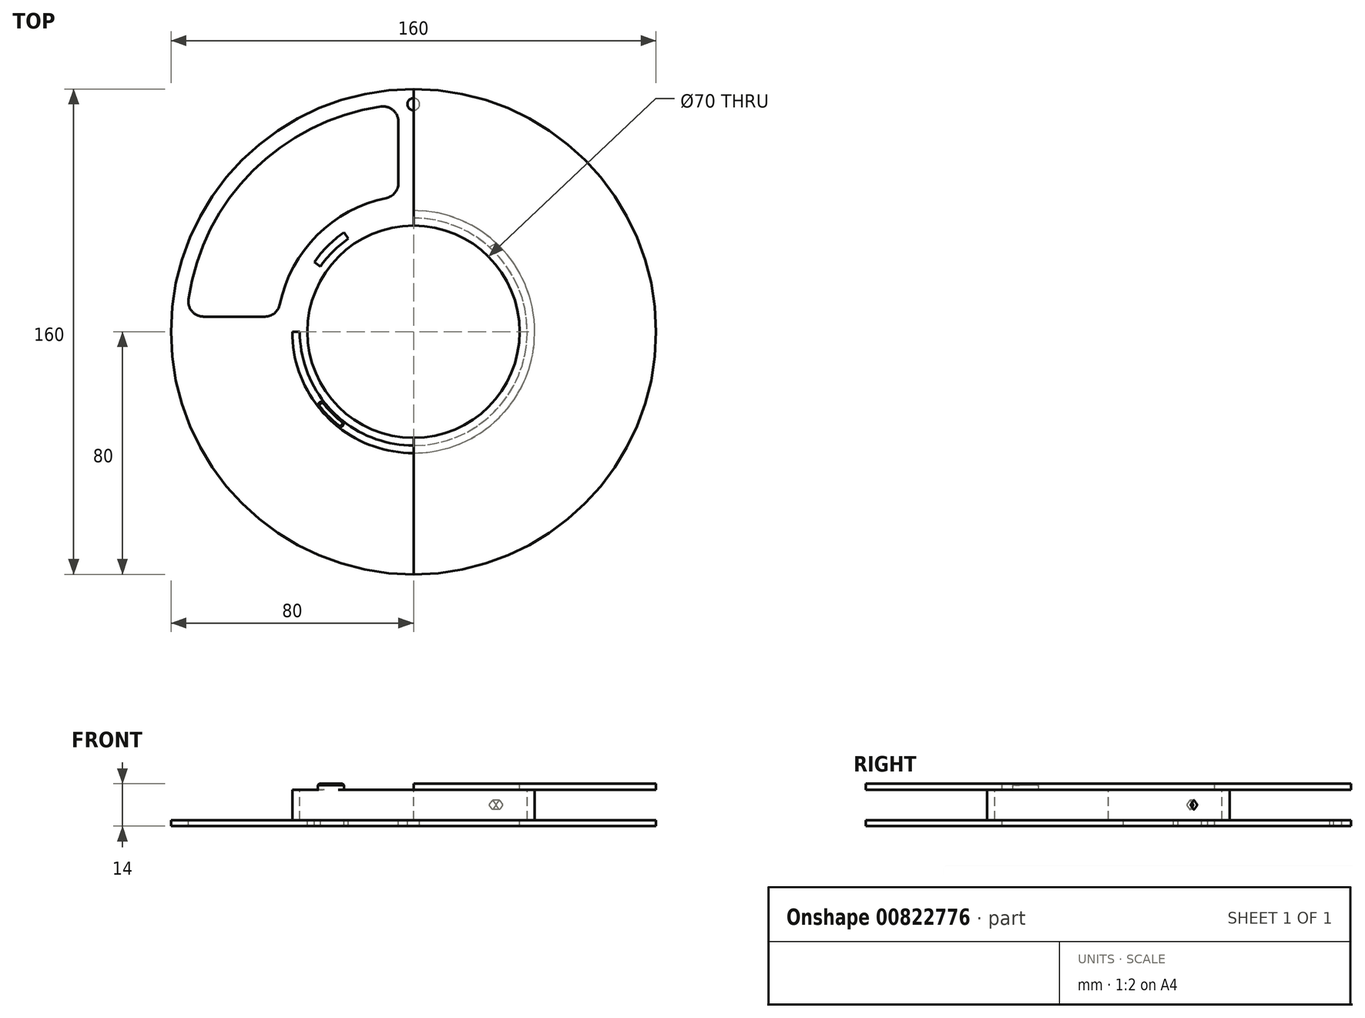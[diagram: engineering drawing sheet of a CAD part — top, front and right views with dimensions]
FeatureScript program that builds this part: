
annotation { "Feature Type Name" : "Feature", "Feature Type Description" : "" }
export const myFeature = defineFeature(function(context is Context, id is Id, definition is map)
    precondition{}
    {
        {
            var Q0;
            Q0=qCreatedBy(makeId("Front.planeOp"),FACE);
            var sketch = newSketch(context, id + "F0", { "sketchPlane" : qUnion([Q0])});
            skLineSegment(sketch, "E0", {"start": v(0, 7) * mm, "end": v(-80, 7) * mm});
            skLineSegment(sketch, "E1", {"start": v(-80, 7) * mm, "end": v(-80, 5) * mm});
            skLineSegment(sketch, "E2", {"start": v(-80, 5) * mm, "end": v(-40, 5) * mm});
            skLineSegment(sketch, "E3", {"start": v(-40, 5) * mm, "end": v(-40, 0) * mm});
            skLineSegment(sketch, "E4", {"start": v(-37.5, 0) * mm, "end": v(-37.5, 5) * mm});
            skLineSegment(sketch, "E5", {"start": v(-37.5, 5) * mm, "end": v(0, 5) * mm});
            skLineSegment(sketch, "E6", {"start": v(0, 5) * mm, "end": v(0, 7) * mm});
            skLineSegment(sketch, "E7.MirrorCS", {"start": v(-80, -7) * mm, "end": v(-80, -5) * mm});
            skLineSegment(sketch, "E8.MirrorCS", {"start": v(0, -7) * mm, "end": v(-80, -7) * mm});
            skLineSegment(sketch, "E9.MirrorCS", {"start": v(-80, -5) * mm, "end": v(-40, -5) * mm});
            skLineSegment(sketch, "E10.MirrorCS", {"start": v(-40, -5) * mm, "end": v(-40, 0) * mm});
            skLineSegment(sketch, "E11.MirrorCS", {"start": v(-37.5, 0) * mm, "end": v(-37.5, -5) * mm});
            skLineSegment(sketch, "E12.MirrorCS", {"start": v(-37.5, -5) * mm, "end": v(0, -5) * mm});
            skLineSegment(sketch, "E13.MirrorCS", {"start": v(0, -5) * mm, "end": v(0, -7) * mm});
            skLineSegment(sketch, "E14", {"start": v(0, 7) * mm, "end": v(0, -7) * mm, "construction": true});
            skSolve(sketch);
        }
        {
            var Q0;
            Q0=qSketchRegion(id+"F0",true);
            var Q1;
            Q1=sQuery(id+"F0.wireOp",EDGE,"E14");
            revolve(context, id + "F1", {"entities" : qUnion([Q0]), "axis" : qUnion([Q1]), "revolveType" : RevolveType.FULL});
        }
        {
            var Q0;
            Q0=makeQuery(id+"F1.opRevolve","SWEPT_FACE",FACE,{"disambiguationData":[OSD([sQuery(id+"F0.wireOp",EDGE,"E0")])]});
            var sketch = newSketch(context, id + "F2", { "sketchPlane" : qUnion([Q0])});
            skLineSegment(sketch, "E15", {"start": v(-40, 0) * mm, "end": v(-80, 0) * mm, "construction": true});
            skPoint(sketch, "E16.orphan", {"position": v(80, 0) * mm});
            skPoint(sketch, "E17.0.start.orphan", {"position": v(0, -80) * mm});
            skArc(sketch, "E18.0", {"start": v(0, 40) * mm, "mid": v(-28.28, 28.28) * mm, "end": v(-40, 0) * mm, "construction": true});
            skArc(sketch, "E19.1", {"start": v(-9, 44.1) * mm, "mid": v(-31.82, 31.82) * mm, "end": v(-44.1, 9) * mm});
            skLineSegment(sketch, "E20", {"start": v(0, 80) * mm, "end": v(0, 40) * mm, "construction": true});
            skPoint(sketch, "E21.visualSharp", {"position": v(-44.72, 5) * mm});
            skArc(sketch, "E21.filletArc", {"start": v(-48.99, 5) * mm, "mid": v(-45.83, 6.13) * mm, "end": v(-44.1, 9) * mm});
            skPoint(sketch, "E22.visualSharp", {"position": v(-73.21, 5) * mm});
            skPoint(sketch, "E23.visualSharp", {"position": v(-5, 73.21) * mm});
            skPoint(sketch, "E24.visualSharp", {"position": v(-5, 44.72) * mm});
            skArc(sketch, "E24.filletArc", {"start": v(-9, 44.1) * mm, "mid": v(-6.13, 45.83) * mm, "end": v(-5, 48.99) * mm});
            skArc(sketch, "E25", {"start": v(0, 80) * mm, "mid": v(-56.57, 56.57) * mm, "end": v(-80, 0) * mm, "construction": true});
            skArc(sketch, "E26.0", {"start": v(-10.71, 74.23) * mm, "mid": v(-53.03, 53.03) * mm, "end": v(-74.23, 10.71) * mm});
            skLineSegment(sketch, "E27", {"start": v(-48.99, 5) * mm, "end": v(-69.28, 5) * mm});
            skLineSegment(sketch, "E28", {"start": v(-5, 48.99) * mm, "end": v(-5, 69.28) * mm});
            skArc(sketch, "E29.filletArc", {"start": v(-5, 69.28) * mm, "mid": v(-6.73, 73.06) * mm, "end": v(-10.71, 74.23) * mm});
            skArc(sketch, "E30.filletArc", {"start": v(-74.23, 10.71) * mm, "mid": v(-73.06, 6.73) * mm, "end": v(-69.28, 5) * mm});
            skSolve(sketch);
        }
        {
            var Q0;
            Q0=qSketchRegion(id+"F2",true);
            extrude(context, id + "F3", {"entities" : qUnion([Q0]), "operationType" : NewBodyOperationType.REMOVE, "endBound" : BoundingType.THROUGH_ALL, "oppositeDirection" : true, "depth" : 25 * mm});
        }
        {
            var Q0;
            Q0=sQuery(id+"F2.wireOp",VERTEX,"E18.0.center");
            var Q1;
            Q1=makeQuery(id+"F1.opRevolve","SWEPT_BODY",BODY,{"disambiguationData":[OSD([sQuery(id+"F0.wireOp",EDGE,"E0"),sQuery(id+"F0.wireOp",EDGE,"E1"),sQuery(id+"F0.wireOp",EDGE,"E2"),sQuery(id+"F0.wireOp",EDGE,"E3"),sQuery(id+"F0.wireOp",EDGE,"E4"),sQuery(id+"F0.wireOp",EDGE,"E5"),sQuery(id+"F0.wireOp",EDGE,"E6"),sQuery(id+"F0.wireOp",EDGE,"E7.MirrorCS"),sQuery(id+"F0.wireOp",EDGE,"E8.MirrorCS"),sQuery(id+"F0.wireOp",EDGE,"E9.MirrorCS"),sQuery(id+"F0.wireOp",EDGE,"E10.MirrorCS"),sQuery(id+"F0.wireOp",EDGE,"E11.MirrorCS"),sQuery(id+"F0.wireOp",EDGE,"E12.MirrorCS"),sQuery(id+"F0.wireOp",EDGE,"E13.MirrorCS")])]});
            hole(context, id + "F4", {"style" : HoleStyle.SIMPLE, "endStyle" : HoleEndStyle.THROUGH, "holeDiameter" : 70 * mm, "isTappedThrough" : true, "tappedDepth" : 38.4 * mm, "tapClearance" : 3, "locations" : qUnion([Q0]), "scope" : qUnion([Q1])});
        }
        {
            var Q0;
            Q0=makeQuery(id+"F2.imprint","IMPRINT",FACE,{"disambiguationData":[TD([[makeQuery(id+"F2.imprint","IMPRINT",EDGE,{"derivedFrom":sQuery(id+"F2.wireOp",EDGE,"E19.1")}),1.0]])]});
            var sketch = newSketch(context, id + "F5", { "sketchPlane" : qUnion([Q0])});
            skLineSegment(sketch, "E31", {"start": v(0, 80) * mm, "end": v(0, 0) * mm});
            skLineSegment(sketch, "E32", {"start": v(0, 0) * mm, "end": v(-80, 0) * mm});
            skLineSegment(sketch, "E33", {"start": v(-80, 0) * mm, "end": v(-80, 80) * mm});
            skLineSegment(sketch, "E34", {"start": v(-80, 80) * mm, "end": v(0, 80) * mm});
            skSolve(sketch);
        }
        {
            var Q0;
            Q0=qSketchRegion(id+"F5",true);
            var Q1;
            Q1=makeQuery(id+"F1.opRevolve","SWEPT_FACE",FACE,{"disambiguationData":[OSD([sQuery(id+"F0.wireOp",EDGE,"E9.MirrorCS")])]});
            extrude(context, id + "F6", {"entities" : qUnion([Q0]), "operationType" : NewBodyOperationType.REMOVE, "endBound" : BoundingType.UP_TO_SURFACE, "oppositeDirection" : true, "endBoundEntityFace" : qUnion([Q1]), "depth" : 25 * mm});
        }
        {
            var Q0;
            Q0=qCreatedBy(makeId("Right.planeOp"),FACE);
            var sketch = newSketch(context, id + "F7", { "sketchPlane" : qUnion([Q0])});
            skPoint(sketch, "E35.0", {"position": v(80, 7) * mm});
            skPoint(sketch, "E36.0", {"position": v(-80, 5) * mm});
            skLineSegment(sketch, "E37.bottom", {"start": v(-80, 5) * mm, "end": v(80, 5) * mm, "construction": true});
            skLineSegment(sketch, "E37.top", {"start": v(-80, 7) * mm, "end": v(80, 7) * mm, "construction": true});
            skLineSegment(sketch, "E37.left", {"start": v(-80, 5) * mm, "end": v(-80, 7) * mm, "construction": true});
            skLineSegment(sketch, "E37.right", {"start": v(80, 5) * mm, "end": v(80, 7) * mm, "construction": true});
            skLineSegment(sketch, "E38.bottom", {"start": v(80, 7) * mm, "end": v(-80, 7) * mm});
            skLineSegment(sketch, "E38.top", {"start": v(80, 5) * mm, "end": v(-80, 5) * mm});
            skLineSegment(sketch, "E38.left", {"start": v(80, 7) * mm, "end": v(80, 5) * mm});
            skLineSegment(sketch, "E38.right", {"start": v(-80, 7) * mm, "end": v(-80, 5) * mm});
            skSolve(sketch);
        }
        {
            var Q0;
            Q0=qSketchRegion(id+"F7",true);
            extrude(context, id + "F8", {"entities" : qUnion([Q0]), "operationType" : NewBodyOperationType.REMOVE, "endBound" : BoundingType.THROUGH_ALL, "oppositeDirection" : true, "depth" : 25 * mm});
        }
        {
            var Q0;
            {var subQ0=sQuery(id+"F0.wireOp",EDGE,"E12.MirrorCS");var subQ1=sQuery(id+"F0.wireOp",EDGE,"E9.MirrorCS");Q0=makeQuery(id+"F5vmHWThCkjWJyu_1.1.F6.boolean.opBoolean","MERGE",FACE,{"derivedFrom":[makeQuery(id+"F6.boolean.opBoolean","MERGE",FACE,{"derivedFrom":[makeQuery(id+"F1.opRevolve","SWEPT_FACE",FACE,{"disambiguationData":[OSD([subQ1])]}),makeQuery(id+"F1.opRevolve","SWEPT_FACE",FACE,{"disambiguationData":[OSD([subQ0])]}),makeQuery(id+"F6.opExtrude","CAP_FACE",FACE,{"disambiguationData":[OSD([subQ1])],"isStart":false})]}),makeQuery(id+"F5vmHWThCkjWJyu_1.1.F6.opExtrude","CAP_FACE",FACE,{"disambiguationData":[OSD([subQ1,subQ0])],"isStart":false})]});}
            var sketch = newSketch(context, id + "F9", { "sketchPlane" : qUnion([Q0])});
            skArc(sketch, "E39.0", {"start": v(0, 40) * mm, "mid": v(-28.28, 28.28) * mm, "end": v(-40, 0) * mm, "construction": true});
            skLineSegment(sketch, "E40", {"start": v(0, 0) * mm, "end": v(-28.28, 28.28) * mm, "construction": true});
            skArc(sketch, "E41", {"start": v(-28.28, 28.28) * mm, "mid": v(-25.71, 30.64) * mm, "end": v(-22.94, 32.77) * mm});
            skArc(sketch, "E42.0", {"start": v(37.5, 0) * mm, "mid": v(26.52, 26.52) * mm, "end": v(0, 37.5) * mm, "construction": true});
            skArc(sketch, "E43", {"start": v(0, 37.5) * mm, "mid": v(-26.52, 26.52) * mm, "end": v(-37.5, 0) * mm, "construction": true});
            skLineSegment(sketch, "E44", {"start": v(-22.94, 32.77) * mm, "end": v(0, 0) * mm, "construction": true});
            skArc(sketch, "E45", {"start": v(-26.52, 26.52) * mm, "mid": v(-24.1, 28.73) * mm, "end": v(-21.5, 30.72) * mm});
            skArc(sketch, "E46.MirrorCS", {"start": v(-37.5, 0) * mm, "mid": v(-26.52, 26.52) * mm, "end": v(0, 37.5) * mm, "construction": true});
            skArc(sketch, "E47.MirrorCS", {"start": v(-40, 0) * mm, "mid": v(-28.28, 28.28) * mm, "end": v(0, 40) * mm, "construction": true});
            skArc(sketch, "E48", {"start": v(-32.77, 22.94) * mm, "mid": v(-30.64, 25.71) * mm, "end": v(-28.28, 28.28) * mm});
            skLineSegment(sketch, "E49", {"start": v(-32.77, 22.94) * mm, "end": v(0, 0) * mm, "construction": true});
            skArc(sketch, "E50", {"start": v(-30.72, 21.5) * mm, "mid": v(-28.73, 24.1) * mm, "end": v(-26.52, 26.52) * mm});
            skLineSegment(sketch, "E51", {"start": v(-30.72, 21.5) * mm, "end": v(-32.77, 22.94) * mm});
            skLineSegment(sketch, "E52", {"start": v(-22.94, 32.77) * mm, "end": v(-21.5, 30.72) * mm});
            skSolve(sketch);
        }
        {
            var Q0;
            Q0=qSketchRegion(id+"F9",true);
            extrude(context, id + "F10", {"entities" : qUnion([Q0]), "operationType" : NewBodyOperationType.REMOVE, "endBound" : BoundingType.THROUGH_ALL, "oppositeDirection" : true, "depth" : 25 * mm});
        }
        {
            var Q0;
            Q0=makeQuery(id+"F2.imprint","IMPRINT",FACE,{"disambiguationData":[TD([[makeQuery(id+"F2.imprint","IMPRINT",EDGE,{"derivedFrom":sQuery(id+"F2.wireOp",EDGE,"E19.1")}),1.0]])]});
            var sketch = newSketch(context, id + "F11", { "sketchPlane" : qUnion([Q0])});
            skArc(sketch, "E53.0", {"start": v(-37.5, 0) * mm, "mid": v(-26.52, -26.52) * mm, "end": v(0, -37.5) * mm, "construction": true});
            skArc(sketch, "E54.0", {"start": v(-40, 0) * mm, "mid": v(-28.28, -28.28) * mm, "end": v(0, -40) * mm, "construction": true});
            skLineSegment(sketch, "E55", {"start": v(-28.28, -28.28) * mm, "end": v(0, 0) * mm, "construction": true});
            skLineSegment(sketch, "E56", {"start": v(-24.07, -31.95) * mm, "end": v(0, 0) * mm, "construction": true});
            skLineSegment(sketch, "E57", {"start": v(-31.95, -24.07) * mm, "end": v(0, 0) * mm, "construction": true});
            skArc(sketch, "E58", {"start": v(-24.07, -31.95) * mm, "mid": v(-28.28, -28.28) * mm, "end": v(-31.95, -24.07) * mm});
            skArc(sketch, "E59", {"start": v(-22.57, -29.95) * mm, "mid": v(-26.52, -26.52) * mm, "end": v(-29.95, -22.57) * mm});
            skLineSegment(sketch, "E60", {"start": v(-31.95, -24.07) * mm, "end": v(-29.95, -22.57) * mm});
            skLineSegment(sketch, "E61", {"start": v(-22.57, -29.95) * mm, "end": v(-24.07, -31.95) * mm});
            skSolve(sketch);
        }
        {
            var Q0;
            Q0=qSketchRegion(id+"F11",true);
            var Q1;
            Q1=makeQuery(id+"F8.boolean.opBoolean","COPY",FACE,{"derivedFrom":makeQuery(id+"F8.opExtrude","SWEPT_FACE",FACE,{"disambiguationData":[OSD([sQuery(id+"F7.wireOp",EDGE,"E38.top")])]})});
            extrude(context, id + "F12", {"entities" : qUnion([Q0]), "operationType" : NewBodyOperationType.ADD, "endBound" : BoundingType.UP_TO_SURFACE, "oppositeDirection" : true, "endBoundEntityFace" : qUnion([Q1]), "depth" : 25 * mm});
        }
        {
            var Q0;
            Q0=makeQuery(id+"F12.opExtrude","SWEPT_EDGE",EDGE,{"disambiguationData":[OSD([sQuery(id+"F11.wireOp",EDGE,"E58"),sQuery(id+"F11.wireOp",EDGE,"E60")])]});
            var Q1;
            Q1=makeQuery(id+"F12.opExtrude","SWEPT_EDGE",EDGE,{"disambiguationData":[OSD([sQuery(id+"F11.wireOp",EDGE,"E58"),sQuery(id+"F11.wireOp",EDGE,"E61")])]});
            var Q2;
            Q2=makeQuery(id+"F12.opExtrude","SWEPT_EDGE",EDGE,{"disambiguationData":[OSD([sQuery(id+"F11.wireOp",EDGE,"E59"),sQuery(id+"F11.wireOp",EDGE,"E60")])]});
            var Q3;
            Q3=makeQuery(id+"F12.opExtrude","SWEPT_EDGE",EDGE,{"disambiguationData":[OSD([sQuery(id+"F11.wireOp",EDGE,"E59"),sQuery(id+"F11.wireOp",EDGE,"E61")])]});
            fillet(context, id + "F13", {"entities" : qUnion([Q0, Q1, Q2, Q3]), "radius" : 1 * mm, "tangentPropagation" : true, "allowEdgeOverflow" : false});
        }
        {
            var Q0;
            Q0=makeQuery(id+"F12.opExtrude","CAP_EDGE",EDGE,{"disambiguationData":[OSD([sQuery(id+"F11.wireOp",EDGE,"E58")])],"isStart":true});
            var Q1;
            Q1=makeQuery(id+"F12.opExtrude","CAP_EDGE",EDGE,{"disambiguationData":[OSD([sQuery(id+"F11.wireOp",EDGE,"E59")])],"isStart":true});
            var Q2;
            Q2=makeQuery(id+"F12.opExtrude","CAP_EDGE",EDGE,{"disambiguationData":[OSD([sQuery(id+"F11.wireOp",EDGE,"E61")])],"isStart":true});
            var Q3;
            Q3=makeQuery(id+"F12.opExtrude","CAP_EDGE",EDGE,{"disambiguationData":[OSD([sQuery(id+"F11.wireOp",EDGE,"E60")])],"isStart":true});
            var Q4;
            Q4=makeQuery(id+"F10.boolean.opBoolean","COPY",EDGE,{"derivedFrom":makeQuery(id+"F10.opExtrude","CAP_EDGE",EDGE,{"disambiguationData":[OSD([sQuery(id+"F9.wireOp",EDGE,"E45"),sQuery(id+"F9.wireOp",EDGE,"E50")])],"isStart":true})});
            var Q5;
            Q5=makeQuery(id+"F10.boolean.opBoolean","COPY",EDGE,{"derivedFrom":makeQuery(id+"F10.opExtrude","CAP_EDGE",EDGE,{"disambiguationData":[OSD([sQuery(id+"F9.wireOp",EDGE,"E51")])],"isStart":true})});
            var Q6;
            Q6=makeQuery(id+"F10.boolean.opBoolean","COPY",EDGE,{"derivedFrom":makeQuery(id+"F10.opExtrude","CAP_EDGE",EDGE,{"disambiguationData":[OSD([sQuery(id+"F9.wireOp",EDGE,"E41"),sQuery(id+"F9.wireOp",EDGE,"E48")])],"isStart":true})});
            var Q7;
            Q7=makeQuery(id+"F10.boolean.opBoolean","COPY",EDGE,{"derivedFrom":makeQuery(id+"F10.opExtrude","CAP_EDGE",EDGE,{"disambiguationData":[OSD([sQuery(id+"F9.wireOp",EDGE,"E52")])],"isStart":true})});
            chamfer(context, id + "F14", {"entities" : qUnion([Q0, Q1, Q2, Q3, Q4, Q5, Q6, Q7]), "width" : .5 * mm, "tangentPropagation" : true});
        }
        {
            var Q0;
            Q0=sQuery(id+"F0.wireOp",EDGE,"E14");
            var Q1;
            Q1=qCreatedBy(makeId("Right.planeOp"),FACE);
            cPlane(context, id + "F15", {"entities" : qUnion([Q0, Q1]), "cplaneType" : CPlaneType.LINE_ANGLE, "offset" : 25 * mm, "angle" : 330 * degree, "width" : 150 * mm, "height" : 150 * mm});
        }
        {
            var Q0;
            Q0=qCreatedBy(id+"F15.planeOp",FACE);
            var sketch = newSketch(context, id + "F16", { "sketchPlane" : qUnion([Q0])});
            skLineSegment(sketch, "E62", {"start": v(-11.51, 0.35) * mm, "end": v(-10.42, 1.44) * mm});
            skLineSegment(sketch, "E63", {"start": v(-10.14, 1.44) * mm, "end": v(-9.05, 0.35) * mm});
            skLineSegment(sketch, "E64", {"start": v(-9.05, -0.35) * mm, "end": v(-10.14, -1.44) * mm});
            skLineSegment(sketch, "E65", {"start": v(-10.42, -1.44) * mm, "end": v(-11.51, -0.35) * mm});
            skPoint(sketch, "E66.visualSharp", {"position": v(-11.87, 0) * mm});
            skArc(sketch, "E66.filletArc", {"start": v(-11.51, 0.35) * mm, "mid": v(-11.66, 0) * mm, "end": v(-11.51, -0.35) * mm});
            skPoint(sketch, "E67.visualSharp", {"position": v(-10.28, -1.59) * mm});
            skArc(sketch, "E67.filletArc", {"start": v(-10.42, -1.44) * mm, "mid": v(-10.28, -1.5) * mm, "end": v(-10.14, -1.44) * mm});
            skPoint(sketch, "E68.visualSharp", {"position": v(-8.7, 0) * mm});
            skArc(sketch, "E68.filletArc", {"start": v(-9.05, -0.35) * mm, "mid": v(-8.9, 0) * mm, "end": v(-9.05, 0.35) * mm});
            skPoint(sketch, "E69.visualSharp", {"position": v(-10.28, 1.59) * mm});
            skArc(sketch, "E69.filletArc", {"start": v(-10.14, 1.44) * mm, "mid": v(-10.28, 1.5) * mm, "end": v(-10.42, 1.44) * mm});
            skSolve(sketch);
        }
        {
            var Q0;
            Q0=makeQuery(id+"F16.imprint","IMPRINT",FACE,{"disambiguationData":[TD([[makeQuery(id+"F16.imprint","IMPRINT",EDGE,{"derivedFrom":sQuery(id+"F16.wireOp",EDGE,"E62")}),-1.0]])]});
            extrude(context, id + "F17", {"entities" : qUnion([Q0]), "operationType" : NewBodyOperationType.REMOVE, "endBound" : BoundingType.THROUGH_ALL, "oppositeDirection" : true, "depth" : 25 * mm});
        }
        {
            var Q0;
            Q0=qCreatedBy(makeId("Top.planeOp"),FACE);
            var sketch = newSketch(context, id + "F18", { "sketchPlane" : qUnion([Q0])});
            skLineSegment(sketch, "E70", {"start": v(0, 87.17) * mm, "end": v(0, 0) * mm, "construction": true});
            skPoint(sketch, "E71", {"position": v(0, 75) * mm});
            skSolve(sketch);
        }
        {
            var Q0;
            Q0=sQuery(id+"F18.wireOp",VERTEX,"E71");
            var Q1;
            Q1=makeQuery(id+"F1.opRevolve","SWEPT_BODY",BODY,{"disambiguationData":[OSD([sQuery(id+"F0.wireOp",EDGE,"E0"),sQuery(id+"F0.wireOp",EDGE,"E1"),sQuery(id+"F0.wireOp",EDGE,"E2"),sQuery(id+"F0.wireOp",EDGE,"E3"),sQuery(id+"F0.wireOp",EDGE,"E4"),sQuery(id+"F0.wireOp",EDGE,"E5"),sQuery(id+"F0.wireOp",EDGE,"E6"),sQuery(id+"F0.wireOp",EDGE,"E7.MirrorCS"),sQuery(id+"F0.wireOp",EDGE,"E8.MirrorCS"),sQuery(id+"F0.wireOp",EDGE,"E9.MirrorCS"),sQuery(id+"F0.wireOp",EDGE,"E10.MirrorCS"),sQuery(id+"F0.wireOp",EDGE,"E11.MirrorCS"),sQuery(id+"F0.wireOp",EDGE,"E12.MirrorCS"),sQuery(id+"F0.wireOp",EDGE,"E13.MirrorCS")])]});
            hole(context, id + "F19", {"style" : HoleStyle.SIMPLE, "endStyle" : HoleEndStyle.THROUGH, "holeDiameter" : 4 * mm, "isTappedThrough" : true, "tappedDepth" : 38.4 * mm, "tapClearance" : 3, "locations" : qUnion([Q0]), "scope" : qUnion([Q1])});
        }
    });
